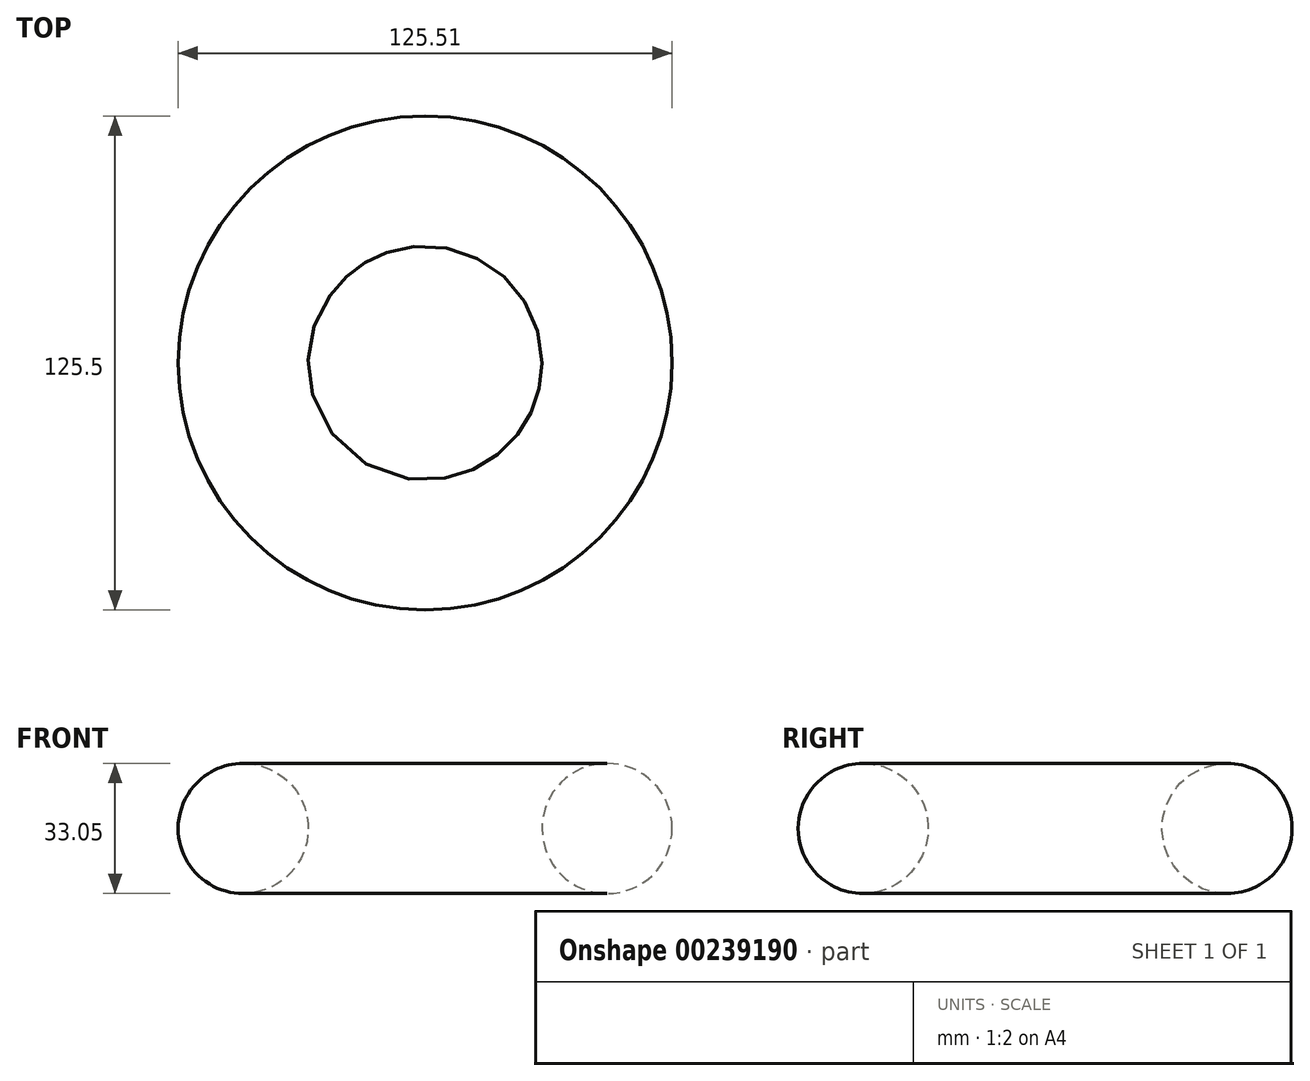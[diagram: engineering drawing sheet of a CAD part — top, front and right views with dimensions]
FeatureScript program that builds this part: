
annotation { "Feature Type Name" : "Feature", "Feature Type Description" : "" }
export const myFeature = defineFeature(function(context is Context, id is Id, definition is map)
    precondition{}
    {
        {
            var Q0;
            Q0=qCreatedBy(makeId("Front.planeOp"),FACE);
            var sketch = newSketch(context, id + "F0", { "sketchPlane" : qUnion([Q0])});
            skCircle(sketch, "E0", {"center": v(32.32, -17.33) * mm, "radius": 16.53 * mm});
            skLineSegment(sketch, "E1", {"start": v(-13.9, -8.52) * mm, "end": v(-13.9, -39.47) * mm, "construction": true});
            skSolve(sketch);
        }
        {
            var Q0;
            Q0=makeQuery(id+"F0.imprint","IMPRINT",FACE,{"disambiguationData":[TD([[makeQuery(id+"F0.imprint","IMPRINT",EDGE,{"derivedFrom":sQuery(id+"F0.wireOp",EDGE,"E0")}),1.0]])]});
            var Q1;
            Q1=sQuery(id+"F0.wireOp",EDGE,"E1");
            revolve(context, id + "F1", {"entities" : qUnion([Q0]), "axis" : qUnion([Q1]), "revolveType" : RevolveType.FULL});
        }
    });
